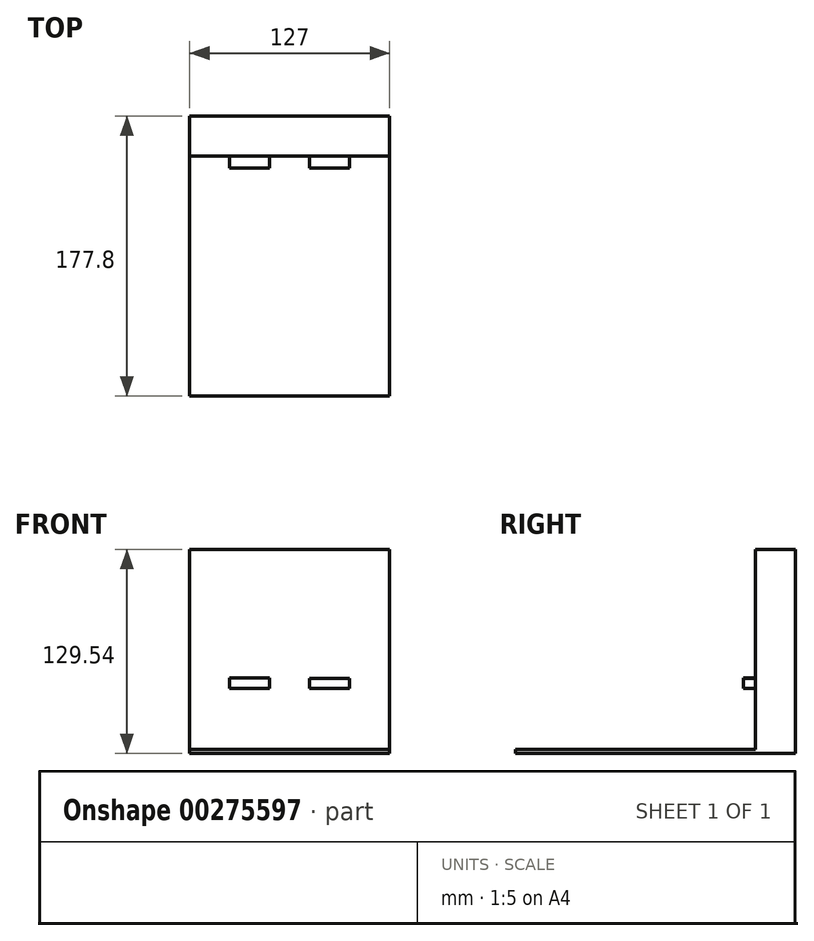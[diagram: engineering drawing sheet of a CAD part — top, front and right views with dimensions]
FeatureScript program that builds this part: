
annotation { "Feature Type Name" : "Feature", "Feature Type Description" : "" }
export const myFeature = defineFeature(function(context is Context, id is Id, definition is map)
    precondition{}
    {
        {
            var Q0;
            Q0=qCreatedBy(makeId("Top.planeOp"),FACE);
            var sketch = newSketch(context, id + "F0", { "sketchPlane" : qUnion([Q0])});
            skLineSegment(sketch, "E0.bottom", {"start": v(63.5, 88.9) * mm, "end": v(-63.5, 88.9) * mm});
            skLineSegment(sketch, "E0.top", {"start": v(63.5, -88.9) * mm, "end": v(-63.5, -88.9) * mm});
            skLineSegment(sketch, "E0.left", {"start": v(63.5, 88.9) * mm, "end": v(63.5, -88.9) * mm});
            skLineSegment(sketch, "E0.right", {"start": v(-63.5, 88.9) * mm, "end": v(-63.5, -88.9) * mm});
            skPoint(sketch, "E0.middle", {"position": v(0, 0) * mm});
            skSolve(sketch);
        }
        {
            var Q0;
            Q0=makeQuery(id+"F0.imprint","IMPRINT",FACE,{"disambiguationData":[TD([[makeQuery(id+"F0.imprint","IMPRINT",EDGE,{"derivedFrom":sQuery(id+"F0.wireOp",EDGE,"E0.bottom")}),1.0]])]});
            extrude(context, id + "F1", {"entities" : qUnion([Q0]), "oppositeDirection" : true, "depth" : 2.54 * mm});
        }
        {
            var Q0;
            Q0=makeQuery(id+"F1.opExtrude","CAP_FACE",FACE,{"disambiguationData":[OSD([sQuery(id+"F0.wireOp",EDGE,"E0.bottom"),sQuery(id+"F0.wireOp",EDGE,"E0.top"),sQuery(id+"F0.wireOp",EDGE,"E0.left"),sQuery(id+"F0.wireOp",EDGE,"E0.right")])],"isStart":true});
            var sketch = newSketch(context, id + "F2", { "sketchPlane" : qUnion([Q0])});
            skLineSegment(sketch, "E1.bottom", {"start": v(-63.5, 88.9) * mm, "end": v(63.5, 88.9) * mm});
            skLineSegment(sketch, "E1.top", {"start": v(-63.5, 63.5) * mm, "end": v(63.5, 63.5) * mm});
            skLineSegment(sketch, "E1.left", {"start": v(-63.5, 88.9) * mm, "end": v(-63.5, 63.5) * mm});
            skLineSegment(sketch, "E1.right", {"start": v(63.5, 88.9) * mm, "end": v(63.5, 63.5) * mm});
            skSolve(sketch);
        }
        {
            var Q0;
            Q0=makeQuery(id+"F2.imprint","IMPRINT",FACE,{"disambiguationData":[TD([[makeQuery(id+"F2.imprint","IMPRINT",EDGE,{"derivedFrom":sQuery(id+"F2.wireOp",EDGE,"E1.bottom")}),1.0]])]});
            extrude(context, id + "F3", {"entities" : qUnion([Q0]), "operationType" : NewBodyOperationType.ADD, "depth" : 127 * mm});
        }
        {
            var Q0;
            Q0=makeQuery(id+"F3.opExtrude","SWEPT_FACE",FACE,{"disambiguationData":[OSD([sQuery(id+"F2.wireOp",EDGE,"E1.top")])]});
            var sketch = newSketch(context, id + "F4", { "sketchPlane" : qUnion([Q0])});
            skLineSegment(sketch, "E2.bottom", {"start": v(-12.7, 38.73) * mm, "end": v(-38.1, 38.73) * mm});
            skLineSegment(sketch, "E2.top", {"start": v(-12.7, 45.58) * mm, "end": v(-38.1, 45.58) * mm});
            skLineSegment(sketch, "E2.left", {"start": v(-12.7, 38.73) * mm, "end": v(-12.7, 45.58) * mm});
            skLineSegment(sketch, "E2.right", {"start": v(-38.1, 38.73) * mm, "end": v(-38.1, 45.58) * mm});
            skPoint(sketch, "E2.middle", {"position": v(-25.4, 42.16) * mm});
            skLineSegment(sketch, "E3.bottom", {"start": v(38.1, 38.74) * mm, "end": v(12.7, 38.73) * mm});
            skLineSegment(sketch, "E3.top", {"start": v(38.1, 45.1) * mm, "end": v(12.7, 45.1) * mm});
            skLineSegment(sketch, "E3.left", {"start": v(38.1, 38.74) * mm, "end": v(38.1, 45.1) * mm});
            skLineSegment(sketch, "E3.right", {"start": v(12.7, 38.73) * mm, "end": v(12.7, 45.1) * mm});
            skPoint(sketch, "E3.middle", {"position": v(25.4, 41.92) * mm});
            skSolve(sketch);
        }
        {
            var Q0;
            Q0=makeQuery(id+"F4.imprint","IMPRINT",FACE,{"disambiguationData":[TD([[makeQuery(id+"F4.imprint","IMPRINT",EDGE,{"derivedFrom":sQuery(id+"F4.wireOp",EDGE,"E2.bottom")}),-1.0]])]});
            var Q1;
            Q1=makeQuery(id+"F4.imprint","IMPRINT",FACE,{"disambiguationData":[TD([[makeQuery(id+"F4.imprint","IMPRINT",EDGE,{"derivedFrom":sQuery(id+"F4.wireOp",EDGE,"E3.bottom")}),-1.0]])]});
            extrude(context, id + "F5", {"entities" : qUnion([Q0, Q1]), "operationType" : NewBodyOperationType.ADD, "depth" : 7.62 * mm});
        }
    });
